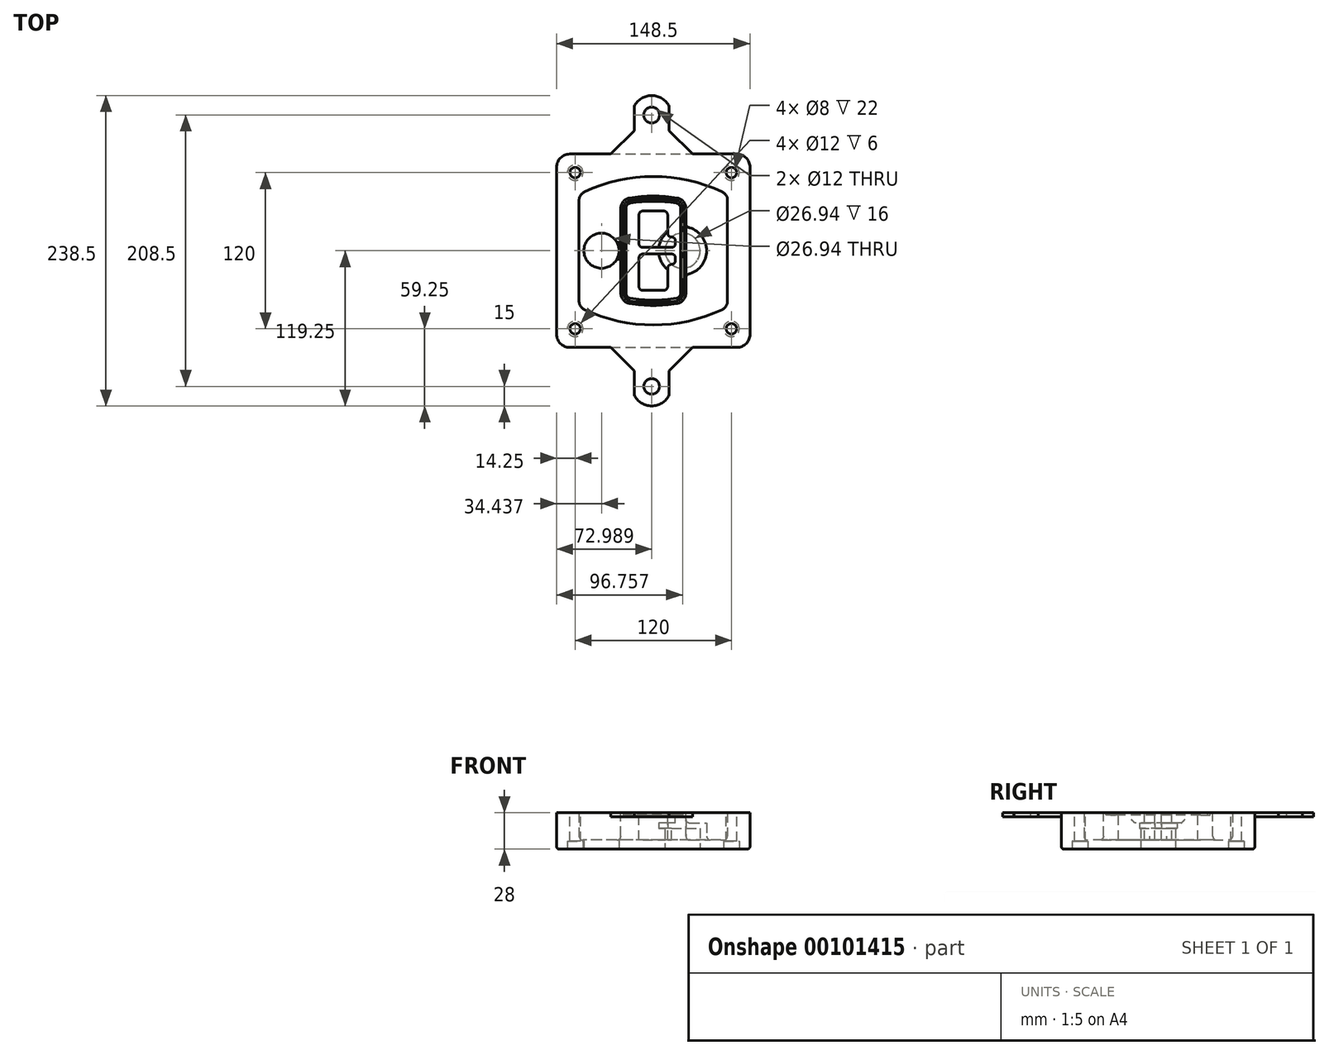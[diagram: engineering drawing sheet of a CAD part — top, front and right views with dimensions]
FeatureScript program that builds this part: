
annotation { "Feature Type Name" : "Feature", "Feature Type Description" : "" }
export const myFeature = defineFeature(function(context is Context, id is Id, definition is map)
    precondition{}
    {
        {
            var Q0;
            Q0=qCreatedBy(makeId("Top.planeOp"),FACE);
            var sketch = newSketch(context, id + "F0", { "sketchPlane" : qUnion([Q0])});
            skPoint(sketch, "E0.rect.middle", {"position": v(0, 0) * mm});
            skLineSegment(sketch, "E1.bottom", {"start": v(-64.25, -74.25) * mm, "end": v(64.25, -74.25) * mm});
            skLineSegment(sketch, "E1.top", {"start": v(-64.25, 74.25) * mm, "end": v(64.25, 74.25) * mm});
            skLineSegment(sketch, "E1.left", {"start": v(-74.25, -64.25) * mm, "end": v(-74.25, 64.25) * mm});
            skLineSegment(sketch, "E1.right", {"start": v(74.25, -64.25) * mm, "end": v(74.25, 64.25) * mm});
            skLineSegment(sketch, "E2", {"start": v(-74.25, 74.25) * mm, "end": v(74.25, -74.25) * mm, "construction": true});
            skLineSegment(sketch, "E3", {"start": v(74.25, 74.25) * mm, "end": v(-74.25, -74.25) * mm, "construction": true});
            skCircle(sketch, "E4", {"center": v(-60, 60) * mm, "radius": 4 * mm});
            skCircle(sketch, "E5", {"center": v(60, 60) * mm, "radius": 4 * mm});
            skCircle(sketch, "E6", {"center": v(60, -60) * mm, "radius": 4 * mm});
            skCircle(sketch, "E7", {"center": v(-60, -60) * mm, "radius": 4 * mm});
            skLineSegment(sketch, "E8", {"start": v(-60, 60) * mm, "end": v(60, 60) * mm, "construction": true});
            skLineSegment(sketch, "E9", {"start": v(60, 60) * mm, "end": v(60, -60) * mm, "construction": true});
            skLineSegment(sketch, "E10", {"start": v(60, -60) * mm, "end": v(-60, -60) * mm, "construction": true});
            skLineSegment(sketch, "E11", {"start": v(-60, -60) * mm, "end": v(-60, 60) * mm, "construction": true});
            skLineSegment(sketch, "E12", {"start": v(-60, 38.83) * mm, "end": v(-60, -38.83) * mm});
            skLineSegment(sketch, "E13", {"start": v(60, 38.83) * mm, "end": v(60, -38.83) * mm});
            skArc(sketch, "E14", {"start": v(54.26, 47.88) * mm, "mid": v(0, 60) * mm, "end": v(-54.26, 47.88) * mm});
            skArc(sketch, "E15", {"start": v(-54.26, -47.88) * mm, "mid": v(0, -60) * mm, "end": v(54.26, -47.88) * mm});
            skLineSegment(sketch, "E16", {"start": v(-60, 0) * mm, "end": v(60, 0) * mm, "construction": true});
            skPoint(sketch, "E17.visualSharp", {"position": v(-60, -45) * mm});
            skArc(sketch, "E17.filletArc", {"start": v(-60, -38.83) * mm, "mid": v(-58.44, -44.2) * mm, "end": v(-54.26, -47.88) * mm});
            skPoint(sketch, "E18.visualSharp", {"position": v(-60, 45) * mm});
            skArc(sketch, "E18.filletArc", {"start": v(-54.26, 47.88) * mm, "mid": v(-58.44, 44.2) * mm, "end": v(-60, 38.83) * mm});
            skPoint(sketch, "E19.visualSharp", {"position": v(60, 45) * mm});
            skArc(sketch, "E19.filletArc", {"start": v(60, 38.83) * mm, "mid": v(58.44, 44.2) * mm, "end": v(54.26, 47.88) * mm});
            skPoint(sketch, "E20.visualSharp", {"position": v(60, -45) * mm});
            skArc(sketch, "E20.filletArc", {"start": v(54.26, -47.88) * mm, "mid": v(58.44, -44.2) * mm, "end": v(60, -38.83) * mm});
            skPoint(sketch, "E21.visualSharp", {"position": v(-74.25, 74.25) * mm});
            skArc(sketch, "E21.filletArc", {"start": v(-64.25, 74.25) * mm, "mid": v(-71.32, 71.32) * mm, "end": v(-74.25, 64.25) * mm});
            skPoint(sketch, "E22.visualSharp", {"position": v(74.25, 74.25) * mm});
            skArc(sketch, "E22.filletArc", {"start": v(74.25, 64.25) * mm, "mid": v(71.32, 71.32) * mm, "end": v(64.25, 74.25) * mm});
            skPoint(sketch, "E23.visualSharp", {"position": v(74.25, -74.25) * mm});
            skArc(sketch, "E23.filletArc", {"start": v(64.25, -74.25) * mm, "mid": v(71.32, -71.32) * mm, "end": v(74.25, -64.25) * mm});
            skPoint(sketch, "E24.visualSharp", {"position": v(-74.25, -74.25) * mm});
            skArc(sketch, "E24.filletArc", {"start": v(-74.25, -64.25) * mm, "mid": v(-71.32, -71.32) * mm, "end": v(-64.25, -74.25) * mm});
            skArc(sketch, "E25.0", {"start": v(57, 38.83) * mm, "mid": v(55.9, 42.58) * mm, "end": v(52.98, 45.17) * mm});
            skLineSegment(sketch, "E25.1", {"start": v(57, 38.83) * mm, "end": v(57, -38.83) * mm});
            skArc(sketch, "E25.2", {"start": v(52.98, -45.17) * mm, "mid": v(55.9, -42.58) * mm, "end": v(57, -38.83) * mm});
            skArc(sketch, "E25.3", {"start": v(-52.98, -45.17) * mm, "mid": v(0, -57) * mm, "end": v(52.98, -45.17) * mm});
            skArc(sketch, "E25.4", {"start": v(-57, -38.83) * mm, "mid": v(-55.9, -42.58) * mm, "end": v(-52.98, -45.17) * mm});
            skArc(sketch, "E25.5", {"start": v(52.98, 45.17) * mm, "mid": v(0, 57) * mm, "end": v(-52.98, 45.17) * mm});
            skLineSegment(sketch, "E25.6", {"start": v(-57, 38.83) * mm, "end": v(-57, -38.83) * mm});
            skArc(sketch, "E25.7", {"start": v(-52.98, 45.17) * mm, "mid": v(-55.9, 42.58) * mm, "end": v(-57, 38.83) * mm});
            skArc(sketch, "E26.0", {"start": v(-55.96, 51.5) * mm, "mid": v(-61.82, 46.33) * mm, "end": v(-64, 38.83) * mm});
            skArc(sketch, "E26.1", {"start": v(55.96, 51.5) * mm, "mid": v(0, 64) * mm, "end": v(-55.96, 51.5) * mm});
            skArc(sketch, "E26.2", {"start": v(64, 38.83) * mm, "mid": v(61.82, 46.33) * mm, "end": v(55.96, 51.5) * mm});
            skLineSegment(sketch, "E26.3", {"start": v(64, 38.83) * mm, "end": v(64, -38.83) * mm});
            skArc(sketch, "E26.4", {"start": v(55.96, -51.5) * mm, "mid": v(61.82, -46.33) * mm, "end": v(64, -38.83) * mm});
            skLineSegment(sketch, "E26.5", {"start": v(-64, 38.83) * mm, "end": v(-64, -38.83) * mm});
            skArc(sketch, "E26.6", {"start": v(-55.96, -51.5) * mm, "mid": v(0, -64) * mm, "end": v(55.96, -51.5) * mm});
            skArc(sketch, "E26.7", {"start": v(-64, -38.83) * mm, "mid": v(-61.82, -46.33) * mm, "end": v(-55.96, -51.5) * mm});
            skSolve(sketch);
        }
        {
            var Q0;
            Q0=makeQuery(id+"F0.imprint","IMPRINT",FACE,{"disambiguationData":[TD([[makeQuery(id+"F0.imprint","IMPRINT",EDGE,{"derivedFrom":sQuery(id+"F0.wireOp",EDGE,"E1.bottom")}),1.0]])]});
            var Q1;
            Q1=makeQuery(id+"F0.imprint","IMPRINT",FACE,{"disambiguationData":[TD([[makeQuery(id+"F0.imprint","IMPRINT",EDGE,{"derivedFrom":sQuery(id+"F0.wireOp",EDGE,"E12")}),1.0]])]});
            var Q2;
            Q2=makeQuery(id+"F0.imprint","IMPRINT",FACE,{"disambiguationData":[TD([[makeQuery(id+"F0.imprint","IMPRINT",EDGE,{"derivedFrom":sQuery(id+"F0.wireOp",EDGE,"E25.0")}),1.0]])]});
            var Q3;
            Q3=makeQuery(id+"F0.imprint","IMPRINT",FACE,{"disambiguationData":[TD([[makeQuery(id+"F0.imprint","IMPRINT",EDGE,{"derivedFrom":sQuery(id+"F0.wireOp",EDGE,"E12")}),-1.0]])]});
            extrude(context, id + "F1", {"entities" : qUnion([Q0, Q1, Q2, Q3]), "oppositeDirection" : true, "depth" : 25 * mm});
        }
        {
            var Q0;
            Q0=makeQuery(id+"F0.imprint","IMPRINT",FACE,{"disambiguationData":[TD([[makeQuery(id+"F0.imprint","IMPRINT",EDGE,{"derivedFrom":sQuery(id+"F0.wireOp",EDGE,"E12")}),1.0]])]});
            extrude(context, id + "F2", {"entities" : qUnion([Q0]), "operationType" : NewBodyOperationType.ADD, "depth" : 3 * mm});
        }
        {
            var Q0;
            Q0=makeQuery(id+"F0.imprint","IMPRINT",FACE,{"disambiguationData":[TD([[makeQuery(id+"F0.imprint","IMPRINT",EDGE,{"derivedFrom":sQuery(id+"F0.wireOp",EDGE,"E25.0")}),1.0]])]});
            extrude(context, id + "F3", {"entities" : qUnion([Q0]), "operationType" : NewBodyOperationType.REMOVE, "oppositeDirection" : true, "depth" : 18 * mm});
        }
        {
            var Q0;
            Q0=makeQuery(id+"F2.opExtrude","CAP_FACE",FACE,{"disambiguationData":[OSD([sQuery(id+"F0.wireOp",EDGE,"E12"),sQuery(id+"F0.wireOp",EDGE,"E13"),sQuery(id+"F0.wireOp",EDGE,"E14"),sQuery(id+"F0.wireOp",EDGE,"E15"),sQuery(id+"F0.wireOp",EDGE,"E17.filletArc"),sQuery(id+"F0.wireOp",EDGE,"E18.filletArc"),sQuery(id+"F0.wireOp",EDGE,"E19.filletArc"),sQuery(id+"F0.wireOp",EDGE,"E20.filletArc"),sQuery(id+"F0.wireOp",EDGE,"E25.0"),sQuery(id+"F0.wireOp",EDGE,"E25.1"),sQuery(id+"F0.wireOp",EDGE,"E25.2"),sQuery(id+"F0.wireOp",EDGE,"E25.3"),sQuery(id+"F0.wireOp",EDGE,"E25.4"),sQuery(id+"F0.wireOp",EDGE,"E25.5"),sQuery(id+"F0.wireOp",EDGE,"E25.6"),sQuery(id+"F0.wireOp",EDGE,"E25.7")])],"isStart":false});
            var sketch = newSketch(context, id + "F4", { "sketchPlane" : qUnion([Q0])});
            skArc(sketch, "E27.0", {"start": v(-18.34, -40.45) * mm, "mid": v(0, -42) * mm, "end": v(18.34, -40.45) * mm});
            skArc(sketch, "E28.0", {"start": v(18.34, 40.45) * mm, "mid": v(0, 42) * mm, "end": v(-18.34, 40.45) * mm});
            skLineSegment(sketch, "E29", {"start": v(-25, 32.57) * mm, "end": v(-25, -32.57) * mm});
            skLineSegment(sketch, "E30", {"start": v(25, 32.57) * mm, "end": v(25, -32.57) * mm});
            skLineSegment(sketch, "E31", {"start": v(-25, 39.1) * mm, "end": v(25, 39.1) * mm, "construction": true});
            skLineSegment(sketch, "E32", {"start": v(-25, -39.1) * mm, "end": v(25, -39.1) * mm, "construction": true});
            skPoint(sketch, "E33.visualSharp", {"position": v(-25, 39.1) * mm});
            skArc(sketch, "E33.filletArc", {"start": v(-18.34, 40.45) * mm, "mid": v(-23.11, 37.73) * mm, "end": v(-25, 32.57) * mm});
            skPoint(sketch, "E34.visualSharp", {"position": v(25, 39.1) * mm});
            skArc(sketch, "E34.filletArc", {"start": v(25, 32.57) * mm, "mid": v(23.11, 37.73) * mm, "end": v(18.34, 40.45) * mm});
            skPoint(sketch, "E35.visualSharp", {"position": v(25, -39.1) * mm});
            skArc(sketch, "E35.filletArc", {"start": v(18.34, -40.45) * mm, "mid": v(23.11, -37.73) * mm, "end": v(25, -32.57) * mm});
            skPoint(sketch, "E36.visualSharp", {"position": v(-25, -39.1) * mm});
            skArc(sketch, "E36.filletArc", {"start": v(-25, -32.57) * mm, "mid": v(-23.11, -37.73) * mm, "end": v(-18.34, -40.45) * mm});
            skArc(sketch, "E37.0", {"start": v(52.98, 45.17) * mm, "mid": v(0, 57) * mm, "end": v(-52.98, 45.17) * mm});
            skArc(sketch, "E37.1", {"start": v(-52.98, 45.17) * mm, "mid": v(-55.9, 42.58) * mm, "end": v(-57, 38.83) * mm});
            skLineSegment(sketch, "E37.2", {"start": v(-57, 38.83) * mm, "end": v(-57, -38.83) * mm});
            skArc(sketch, "E37.3", {"start": v(-57, -38.83) * mm, "mid": v(-55.9, -42.58) * mm, "end": v(-52.98, -45.17) * mm});
            skArc(sketch, "E37.4", {"start": v(-52.98, -45.17) * mm, "mid": v(0, -57) * mm, "end": v(52.98, -45.17) * mm});
            skArc(sketch, "E37.5", {"start": v(52.98, -45.17) * mm, "mid": v(55.9, -42.58) * mm, "end": v(57, -38.83) * mm});
            skLineSegment(sketch, "E37.6", {"start": v(57, 38.83) * mm, "end": v(57, -38.83) * mm});
            skArc(sketch, "E37.7", {"start": v(57, 38.83) * mm, "mid": v(55.9, 42.58) * mm, "end": v(52.98, 45.17) * mm});
            skLineSegment(sketch, "E38.0", {"start": v(23, 32.57) * mm, "end": v(23, -32.57) * mm});
            skArc(sketch, "E38.1", {"start": v(18, -38.48) * mm, "mid": v(21.58, -36.44) * mm, "end": v(23, -32.57) * mm});
            skArc(sketch, "E38.2", {"start": v(-18, -38.48) * mm, "mid": v(0, -40) * mm, "end": v(18, -38.48) * mm});
            skArc(sketch, "E38.3", {"start": v(-23, -32.57) * mm, "mid": v(-21.58, -36.44) * mm, "end": v(-18, -38.48) * mm});
            skLineSegment(sketch, "E38.4", {"start": v(-23, 32.57) * mm, "end": v(-23, -32.57) * mm});
            skArc(sketch, "E38.5", {"start": v(23, 32.57) * mm, "mid": v(21.58, 36.44) * mm, "end": v(18, 38.48) * mm});
            skArc(sketch, "E38.6", {"start": v(-18, 38.48) * mm, "mid": v(-21.58, 36.44) * mm, "end": v(-23, 32.57) * mm});
            skArc(sketch, "E38.7", {"start": v(18, 38.48) * mm, "mid": v(0, 40) * mm, "end": v(-18, 38.48) * mm});
            skArc(sketch, "E39.0", {"start": v(21, 32.57) * mm, "mid": v(20.06, 35.15) * mm, "end": v(17.67, 36.5) * mm});
            skLineSegment(sketch, "E39.1", {"start": v(21, 32.57) * mm, "end": v(21, -32.57) * mm});
            skArc(sketch, "E39.2", {"start": v(17.67, -36.5) * mm, "mid": v(20.06, -35.15) * mm, "end": v(21, -32.57) * mm});
            skArc(sketch, "E39.3", {"start": v(-17.67, -36.5) * mm, "mid": v(0, -38) * mm, "end": v(17.67, -36.5) * mm});
            skArc(sketch, "E39.4", {"start": v(-21, -32.57) * mm, "mid": v(-20.06, -35.15) * mm, "end": v(-17.67, -36.5) * mm});
            skArc(sketch, "E39.5", {"start": v(17.67, 36.5) * mm, "mid": v(0, 38) * mm, "end": v(-17.67, 36.5) * mm});
            skLineSegment(sketch, "E39.6", {"start": v(-21, 32.57) * mm, "end": v(-21, -32.57) * mm});
            skArc(sketch, "E39.7", {"start": v(-17.67, 36.5) * mm, "mid": v(-20.06, 35.15) * mm, "end": v(-21, 32.57) * mm});
            skLineSegment(sketch, "E40", {"start": v(-25, 0) * mm, "end": v(25, 0) * mm, "construction": true});
            skLineSegment(sketch, "E41", {"start": v(-11, 5.5) * mm, "end": v(-11, 27.5) * mm});
            skLineSegment(sketch, "E42", {"start": v(-8, 30.5) * mm, "end": v(8, 30.5) * mm});
            skLineSegment(sketch, "E43", {"start": v(11, 27.5) * mm, "end": v(11, 13.5) * mm});
            skLineSegment(sketch, "E44", {"start": v(14, 10.5) * mm, "end": v(14, 10.5) * mm});
            skLineSegment(sketch, "E45", {"start": v(17, 7.5) * mm, "end": v(17, 5.5) * mm});
            skLineSegment(sketch, "E46", {"start": v(14, 2.5) * mm, "end": v(-8, 2.5) * mm});
            skPoint(sketch, "E47.visualSharp", {"position": v(-11, 30.5) * mm});
            skArc(sketch, "E47.filletArc", {"start": v(-8, 30.5) * mm, "mid": v(-10.12, 29.62) * mm, "end": v(-11, 27.5) * mm});
            skPoint(sketch, "E48.visualSharp", {"position": v(11, 30.5) * mm});
            skArc(sketch, "E48.filletArc", {"start": v(11, 27.5) * mm, "mid": v(10.12, 29.62) * mm, "end": v(8, 30.5) * mm});
            skPoint(sketch, "E49.visualSharp", {"position": v(11, 10.5) * mm});
            skArc(sketch, "E49.filletArc", {"start": v(11, 13.5) * mm, "mid": v(11.88, 11.38) * mm, "end": v(14, 10.5) * mm});
            skPoint(sketch, "E50.visualSharp", {"position": v(17, 10.5) * mm});
            skArc(sketch, "E50.filletArc", {"start": v(17, 7.5) * mm, "mid": v(16.12, 9.62) * mm, "end": v(14, 10.5) * mm});
            skPoint(sketch, "E51.visualSharp", {"position": v(17, 2.5) * mm});
            skArc(sketch, "E51.filletArc", {"start": v(14, 2.5) * mm, "mid": v(16.12, 3.38) * mm, "end": v(17, 5.5) * mm});
            skPoint(sketch, "E52.visualSharp", {"position": v(-11, 2.5) * mm});
            skArc(sketch, "E52.filletArc", {"start": v(-11, 5.5) * mm, "mid": v(-10.12, 3.38) * mm, "end": v(-8, 2.5) * mm});
            skLineSegment(sketch, "E53.0.MirrorCS", {"start": v(14, -2.5) * mm, "end": v(-8, -2.5) * mm});
            skArc(sketch, "E54.0.MirrorCS", {"start": v(-11, -5.5) * mm, "mid": v(-10.12, -3.38) * mm, "end": v(-8, -2.5) * mm});
            skLineSegment(sketch, "E55.0.MirrorCS", {"start": v(-11, -5.5) * mm, "end": v(-11, -27.5) * mm});
            skArc(sketch, "E56.0.MirrorCS", {"start": v(-8, -30.5) * mm, "mid": v(-10.12, -29.62) * mm, "end": v(-11, -27.5) * mm});
            skLineSegment(sketch, "E57.0.MirrorCS", {"start": v(-8, -30.5) * mm, "end": v(8, -30.5) * mm});
            skArc(sketch, "E58.0.MirrorCS", {"start": v(11, -27.5) * mm, "mid": v(10.12, -29.62) * mm, "end": v(8, -30.5) * mm});
            skLineSegment(sketch, "E59.0.MirrorCS", {"start": v(11, -27.5) * mm, "end": v(11, -13.5) * mm});
            skArc(sketch, "E60.0.MirrorCS", {"start": v(11, -13.5) * mm, "mid": v(11.88, -11.38) * mm, "end": v(14, -10.5) * mm});
            skArc(sketch, "E61.0.MirrorCS", {"start": v(17, -7.5) * mm, "mid": v(16.12, -9.62) * mm, "end": v(14, -10.5) * mm});
            skLineSegment(sketch, "E62.0.MirrorCS", {"start": v(17, -7.5) * mm, "end": v(17, -5.5) * mm});
            skArc(sketch, "E63.0.MirrorCS", {"start": v(14, -2.5) * mm, "mid": v(16.12, -3.38) * mm, "end": v(17, -5.5) * mm});
            skSolve(sketch);
        }
        {
            var Q0;
            Q0=makeQuery(id+"F4.imprint","IMPRINT",FACE,{"disambiguationData":[TD([[makeQuery(id+"F4.imprint","IMPRINT",EDGE,{"derivedFrom":sQuery(id+"F4.wireOp",EDGE,"E27.0")}),1.0]])]});
            var Q1;
            Q1=makeQuery(id+"F4.imprint","IMPRINT",FACE,{"disambiguationData":[TD([[makeQuery(id+"F4.imprint","IMPRINT",EDGE,{"derivedFrom":sQuery(id+"F4.wireOp",EDGE,"E38.0")}),-1.0]])]});
            var Q2;
            Q2=makeQuery(id+"F4.imprint","IMPRINT",FACE,{"disambiguationData":[TD([[makeQuery(id+"F4.imprint","IMPRINT",EDGE,{"derivedFrom":sQuery(id+"F4.wireOp",EDGE,"E39.0")}),1.0]])]});
            extrude(context, id + "F5", {"entities" : qUnion([Q0, Q1, Q2]), "operationType" : NewBodyOperationType.ADD, "endBound" : BoundingType.UP_TO_NEXT, "oppositeDirection" : true, "depth" : 25 * mm});
        }
        {
            var Q0;
            Q0=makeQuery(id+"F4.imprint","IMPRINT",FACE,{"disambiguationData":[TD([[makeQuery(id+"F4.imprint","IMPRINT",EDGE,{"derivedFrom":sQuery(id+"F4.wireOp",EDGE,"E38.0")}),-1.0]])]});
            extrude(context, id + "F6", {"entities" : qUnion([Q0]), "operationType" : NewBodyOperationType.REMOVE, "oppositeDirection" : true, "depth" : 2 * mm});
        }
        {
            var Q0;
            Q0=makeQuery(id+"F1.opExtrude","CAP_FACE",FACE,{"disambiguationData":[OSD([sQuery(id+"F0.wireOp",EDGE,"E1.bottom"),sQuery(id+"F0.wireOp",EDGE,"E1.top"),sQuery(id+"F0.wireOp",EDGE,"E1.left"),sQuery(id+"F0.wireOp",EDGE,"E1.right"),sQuery(id+"F0.wireOp",EDGE,"E4"),sQuery(id+"F0.wireOp",EDGE,"E5"),sQuery(id+"F0.wireOp",EDGE,"E6"),sQuery(id+"F0.wireOp",EDGE,"E7"),sQuery(id+"F0.wireOp",EDGE,"E21.filletArc"),sQuery(id+"F0.wireOp",EDGE,"E22.filletArc"),sQuery(id+"F0.wireOp",EDGE,"E23.filletArc"),sQuery(id+"F0.wireOp",EDGE,"E24.filletArc")])],"isStart":false});
            var sketch = newSketch(context, id + "F7", { "sketchPlane" : qUnion([Q0])});
            skCircle(sketch, "E64", {"center": v(22.5, 0) * mm, "radius": 13.47 * mm});
            skCircle(sketch, "E65", {"center": v(-39.81, 0) * mm, "radius": 13.47 * mm});
            skLineSegment(sketch, "E66", {"start": v(74.25, 0) * mm, "end": v(-74.25, 0) * mm});
            skCircle(sketch, "E67", {"center": v(22.5, 0) * mm, "radius": 18.47 * mm});
            skCircle(sketch, "E68", {"center": v(60, -60) * mm, "radius": 6 * mm});
            skCircle(sketch, "E69", {"center": v(-60, -60) * mm, "radius": 6 * mm});
            skCircle(sketch, "E70", {"center": v(-60, 60) * mm, "radius": 6 * mm});
            skCircle(sketch, "E71", {"center": v(60, 60) * mm, "radius": 6 * mm});
            skSolve(sketch);
        }
        {
            var Q0;
            {var subQ1=sQuery(id+"F7.wireOp",EDGE,"E66");var subQ4=sQuery(id+"F7.wireOp",EDGE,"E64");var subQ6=makeQuery(id+"F7.imprint","INTERSECT",VERTEX,{"disambiguationData":[OD(0.0)],"derivedFrom":[subQ4,subQ1]});Q0=makeQuery(id+"F7.imprint","IMPRINT",FACE,{"disambiguationData":[TD([[makeQuery(id+"F7.imprint","IMPRINT",EDGE,{"disambiguationData":[TD([[subQ6,-1.0]])],"derivedFrom":subQ4}),-1.0]])]});}
            var Q1;
            {var subQ0=sQuery(id+"F7.wireOp",EDGE,"E66");var subQ1=sQuery(id+"F7.wireOp",EDGE,"E64");var subQ3=makeQuery(id+"F7.imprint","INTERSECT",VERTEX,{"disambiguationData":[OD(0.0)],"derivedFrom":[subQ1,subQ0]});Q1=makeQuery(id+"F7.imprint","IMPRINT",FACE,{"disambiguationData":[TD([[makeQuery(id+"F7.imprint","IMPRINT",EDGE,{"disambiguationData":[TD([[subQ3,-1.0]])],"derivedFrom":subQ1}),1.0]])]});}
            var Q2;
            {var subQ0=sQuery(id+"F7.wireOp",EDGE,"E66");var subQ1=sQuery(id+"F7.wireOp",EDGE,"E64");var subQ3=makeQuery(id+"F7.imprint","INTERSECT",VERTEX,{"disambiguationData":[OD(0.0)],"derivedFrom":[subQ1,subQ0]});Q2=makeQuery(id+"F7.imprint","IMPRINT",FACE,{"disambiguationData":[TD([[makeQuery(id+"F7.imprint","IMPRINT",EDGE,{"disambiguationData":[TD([[subQ3,1.0]])],"derivedFrom":subQ1}),1.0]])]});}
            var Q3;
            {var subQ1=sQuery(id+"F7.wireOp",EDGE,"E66");var subQ4=sQuery(id+"F7.wireOp",EDGE,"E64");var subQ6=makeQuery(id+"F7.imprint","INTERSECT",VERTEX,{"disambiguationData":[OD(0.0)],"derivedFrom":[subQ4,subQ1]});Q3=makeQuery(id+"F7.imprint","IMPRINT",FACE,{"disambiguationData":[TD([[makeQuery(id+"F7.imprint","IMPRINT",EDGE,{"disambiguationData":[TD([[subQ6,1.0]])],"derivedFrom":subQ4}),-1.0]])]});}
            extrude(context, id + "F8", {"entities" : qUnion([Q0, Q1, Q2, Q3]), "operationType" : NewBodyOperationType.ADD, "oppositeDirection" : true, "depth" : 20 * mm});
        }
        {
            var Q0;
            {var subQ0=sQuery(id+"F7.wireOp",EDGE,"E66");var subQ1=sQuery(id+"F7.wireOp",EDGE,"E64");var subQ3=makeQuery(id+"F7.imprint","INTERSECT",VERTEX,{"disambiguationData":[OD(0.0)],"derivedFrom":[subQ1,subQ0]});Q0=makeQuery(id+"F7.imprint","IMPRINT",FACE,{"disambiguationData":[TD([[makeQuery(id+"F7.imprint","IMPRINT",EDGE,{"disambiguationData":[TD([[subQ3,-1.0]])],"derivedFrom":subQ1}),1.0]])]});}
            var Q1;
            {var subQ0=sQuery(id+"F7.wireOp",EDGE,"E66");var subQ1=sQuery(id+"F7.wireOp",EDGE,"E64");var subQ3=makeQuery(id+"F7.imprint","INTERSECT",VERTEX,{"disambiguationData":[OD(0.0)],"derivedFrom":[subQ1,subQ0]});Q1=makeQuery(id+"F7.imprint","IMPRINT",FACE,{"disambiguationData":[TD([[makeQuery(id+"F7.imprint","IMPRINT",EDGE,{"disambiguationData":[TD([[subQ3,1.0]])],"derivedFrom":subQ1}),1.0]])]});}
            extrude(context, id + "F9", {"entities" : qUnion([Q0, Q1]), "operationType" : NewBodyOperationType.REMOVE, "oppositeDirection" : true, "depth" : 16 * mm});
        }
        {
            var Q0;
            {var subQ0=sQuery(id+"F7.wireOp",EDGE,"E66");var subQ1=sQuery(id+"F7.wireOp",EDGE,"E65");var subQ3=makeQuery(id+"F7.imprint","INTERSECT",VERTEX,{"disambiguationData":[OD(0.0)],"derivedFrom":[subQ1,subQ0]});Q0=makeQuery(id+"F7.imprint","IMPRINT",FACE,{"disambiguationData":[TD([[makeQuery(id+"F7.imprint","IMPRINT",EDGE,{"disambiguationData":[TD([[subQ3,-1.0]])],"derivedFrom":subQ1}),1.0]])]});}
            var Q1;
            {var subQ0=sQuery(id+"F7.wireOp",EDGE,"E66");var subQ1=sQuery(id+"F7.wireOp",EDGE,"E65");var subQ3=makeQuery(id+"F7.imprint","INTERSECT",VERTEX,{"disambiguationData":[OD(0.0)],"derivedFrom":[subQ1,subQ0]});Q1=makeQuery(id+"F7.imprint","IMPRINT",FACE,{"disambiguationData":[TD([[makeQuery(id+"F7.imprint","IMPRINT",EDGE,{"disambiguationData":[TD([[subQ3,1.0]])],"derivedFrom":subQ1}),1.0]])]});}
            extrude(context, id + "F10", {"entities" : qUnion([Q0, Q1]), "operationType" : NewBodyOperationType.REMOVE, "oppositeDirection" : true, "depth" : 25 * mm});
        }
        {
            var Q0;
            Q0=makeQuery(id+"F7.imprint","IMPRINT",FACE,{"disambiguationData":[TD([[makeQuery(id+"F7.imprint","IMPRINT",EDGE,{"derivedFrom":sQuery(id+"F7.wireOp",EDGE,"E68")}),1.0]])]});
            var Q1;
            Q1=makeQuery(id+"F7.imprint","IMPRINT",FACE,{"disambiguationData":[TD([[makeQuery(id+"F7.imprint","IMPRINT",EDGE,{"derivedFrom":makeQuery(id+"F1.opExtrude","CAP_EDGE",EDGE,{"disambiguationData":[OSD([sQuery(id+"F0.wireOp",EDGE,"E5")])],"isStart":false})}),-1.0]])]});
            var Q2;
            Q2=makeQuery(id+"F7.imprint","IMPRINT",FACE,{"disambiguationData":[TD([[makeQuery(id+"F7.imprint","IMPRINT",EDGE,{"derivedFrom":sQuery(id+"F7.wireOp",EDGE,"E69")}),1.0]])]});
            var Q3;
            Q3=makeQuery(id+"F7.imprint","IMPRINT",FACE,{"disambiguationData":[TD([[makeQuery(id+"F7.imprint","IMPRINT",EDGE,{"derivedFrom":makeQuery(id+"F1.opExtrude","CAP_EDGE",EDGE,{"disambiguationData":[OSD([sQuery(id+"F0.wireOp",EDGE,"E4")])],"isStart":false})}),-1.0]])]});
            var Q4;
            Q4=makeQuery(id+"F7.imprint","IMPRINT",FACE,{"disambiguationData":[TD([[makeQuery(id+"F7.imprint","IMPRINT",EDGE,{"derivedFrom":sQuery(id+"F7.wireOp",EDGE,"E70")}),1.0]])]});
            var Q5;
            Q5=makeQuery(id+"F7.imprint","IMPRINT",FACE,{"disambiguationData":[TD([[makeQuery(id+"F7.imprint","IMPRINT",EDGE,{"derivedFrom":makeQuery(id+"F1.opExtrude","CAP_EDGE",EDGE,{"disambiguationData":[OSD([sQuery(id+"F0.wireOp",EDGE,"E7")])],"isStart":false})}),-1.0]])]});
            var Q6;
            Q6=makeQuery(id+"F7.imprint","IMPRINT",FACE,{"disambiguationData":[TD([[makeQuery(id+"F7.imprint","IMPRINT",EDGE,{"derivedFrom":sQuery(id+"F7.wireOp",EDGE,"E71")}),1.0]])]});
            var Q7;
            Q7=makeQuery(id+"F7.imprint","IMPRINT",FACE,{"disambiguationData":[TD([[makeQuery(id+"F7.imprint","IMPRINT",EDGE,{"derivedFrom":makeQuery(id+"F1.opExtrude","CAP_EDGE",EDGE,{"disambiguationData":[OSD([sQuery(id+"F0.wireOp",EDGE,"E6")])],"isStart":false})}),-1.0]])]});
            extrude(context, id + "F11", {"entities" : qUnion([Q0, Q1, Q2, Q3, Q4, Q5, Q6, Q7]), "operationType" : NewBodyOperationType.REMOVE, "oppositeDirection" : true, "depth" : 6 * mm});
        }
        {
            var Q0;
            Q0=makeQuery(id+"F9.boolean.opBoolean","COPY",FACE,{"derivedFrom":makeQuery(id+"F9.opExtrude","CAP_FACE",FACE,{"disambiguationData":[OSD([sQuery(id+"F7.wireOp",EDGE,"E64")])],"isStart":false})});
            var sketch = newSketch(context, id + "F12", { "sketchPlane" : qUnion([Q0])});
            skArc(sketch, "E72.0", {"start": v(11, 14.45) * mm, "mid": v(6.45, 9.13) * mm, "end": v(4.2, 2.5) * mm});
            skArc(sketch, "E72.1", {"start": v(4.2, -2.5) * mm, "mid": v(6.45, -9.13) * mm, "end": v(11, -14.45) * mm});
            skLineSegment(sketch, "E73", {"start": v(4.2, -2.5) * mm, "end": v(14, -2.5) * mm});
            skLineSegment(sketch, "E74.0", {"start": v(14, 2.5) * mm, "end": v(4.2, 2.5) * mm});
            skArc(sketch, "E74.1", {"start": v(14, 2.5) * mm, "mid": v(16.12, 3.38) * mm, "end": v(17, 5.5) * mm});
            skLineSegment(sketch, "E74.2", {"start": v(17, 7.5) * mm, "end": v(17, 5.5) * mm});
            skArc(sketch, "E74.3", {"start": v(17, 7.5) * mm, "mid": v(16.12, 9.62) * mm, "end": v(14, 10.5) * mm});
            skArc(sketch, "E74.4", {"start": v(11, 13.5) * mm, "mid": v(11.88, 11.38) * mm, "end": v(14, 10.5) * mm});
            skLineSegment(sketch, "E74.5", {"start": v(11, 14.45) * mm, "end": v(11, 13.5) * mm});
            skLineSegment(sketch, "E74.7", {"start": v(14, -2.5) * mm, "end": v(4.2, -2.5) * mm});
            skArc(sketch, "E74.8", {"start": v(14, -2.5) * mm, "mid": v(16.12, -3.38) * mm, "end": v(17, -5.5) * mm});
            skLineSegment(sketch, "E74.9", {"start": v(17, -7.5) * mm, "end": v(17, -5.5) * mm});
            skArc(sketch, "E74.10", {"start": v(17, -7.5) * mm, "mid": v(16.12, -9.62) * mm, "end": v(14, -10.5) * mm});
            skArc(sketch, "E74.11", {"start": v(11, -13.5) * mm, "mid": v(11.88, -11.38) * mm, "end": v(14, -10.5) * mm});
            skLineSegment(sketch, "E74.12", {"start": v(11, -14.45) * mm, "end": v(11, -13.5) * mm});
            skPoint(sketch, "E75.orphan", {"position": v(11, -27.5) * mm});
            skPoint(sketch, "E76.orphan", {"position": v(-8, -2.5) * mm});
            skPoint(sketch, "E77.orphan", {"position": v(-8, 2.5) * mm});
            skPoint(sketch, "E78.orphan", {"position": v(11, 27.5) * mm});
            skSolve(sketch);
        }
        {
            var Q0;
            {var subQ7=sQuery(id+"F12.wireOp",EDGE,"E72.0");var subQ14=sQuery(id+"F12.wireOp",EDGE,"E72.1");var subQ16=sQuery(id+"F12.wireOp",EDGE,"E74.1");var subQ18=sQuery(id+"F12.wireOp",EDGE,"E74.8");Q0=qUnion([makeQuery(id+"F12.imprint","IMPRINT",FACE,{"disambiguationData":[TD([[makeQuery(id+"F12.imprint","IMPRINT",EDGE,{"derivedFrom":subQ7}),1.0]])]}),makeQuery(id+"F12.imprint","IMPRINT",FACE,{"disambiguationData":[TD([[makeQuery(id+"F12.imprint","IMPRINT",EDGE,{"derivedFrom":subQ14}),1.0]])]}),makeQuery(id+"F12.imprint","IMPRINT",FACE,{"disambiguationData":[TD([[makeQuery(id+"F12.imprint","IMPRINT",EDGE,{"derivedFrom":subQ16}),1.0]])]}),makeQuery(id+"F12.imprint","IMPRINT",FACE,{"disambiguationData":[TD([[makeQuery(id+"F12.imprint","IMPRINT",EDGE,{"derivedFrom":subQ18}),-1.0]])]})]);}
            var Q1;
            Q1=makeQuery(id+"F5.boolean.opBoolean","SPLIT",FACE,{"disambiguationData":[TD([makeQuery(id+"F5.opExtrude","SWEPT_FACE",FACE,{"disambiguationData":[OSD([sQuery(id+"F4.wireOp",EDGE,"E41")])]})])],"derivedFrom":makeQuery(id+"F3.boolean.opBoolean","COPY",FACE,{"derivedFrom":makeQuery(id+"F3.opExtrude","CAP_FACE",FACE,{"disambiguationData":[OSD([sQuery(id+"F0.wireOp",EDGE,"E25.0"),sQuery(id+"F0.wireOp",EDGE,"E25.1"),sQuery(id+"F0.wireOp",EDGE,"E25.2"),sQuery(id+"F0.wireOp",EDGE,"E25.3"),sQuery(id+"F0.wireOp",EDGE,"E25.4"),sQuery(id+"F0.wireOp",EDGE,"E25.5"),sQuery(id+"F0.wireOp",EDGE,"E25.6"),sQuery(id+"F0.wireOp",EDGE,"E25.7")])],"isStart":false})})});
            extrude(context, id + "F13", {"entities" : qUnion([Q0]), "operationType" : NewBodyOperationType.REMOVE, "endBound" : BoundingType.UP_TO_SURFACE, "endBoundEntityFace" : qUnion([Q1]), "depth" : 25 * mm});
        }
        {
            var Q0;
            Q0=makeQuery(id+"F3.boolean.opBoolean","COPY",EDGE,{"derivedFrom":makeQuery(id+"F3.opExtrude","CAP_EDGE",EDGE,{"disambiguationData":[OSD([sQuery(id+"F0.wireOp",EDGE,"E25.6")])],"isStart":false})});
            var Q1;
            Q1=makeQuery(id+"F8.boolean.opBoolean","INTERSECT",EDGE,{"derivedFrom":[makeQuery(id+"F5.opExtrude","SWEPT_FACE",FACE,{"disambiguationData":[OSD([sQuery(id+"F4.wireOp",EDGE,"E30")])]}),makeQuery(id+"F8.opExtrude","CAP_FACE",FACE,{"disambiguationData":[OSD([sQuery(id+"F7.wireOp",EDGE,"E67")])],"isStart":false})]});
            var Q2;
            Q2=makeQuery(id+"F8.boolean.opBoolean","INTERSECT",EDGE,{"disambiguationData":[OD(1.0)],"derivedFrom":[makeQuery(id+"F5.opExtrude","SWEPT_FACE",FACE,{"disambiguationData":[OSD([sQuery(id+"F4.wireOp",EDGE,"E30")])]}),makeQuery(id+"F8.opExtrude","SWEPT_FACE",FACE,{"disambiguationData":[OSD([sQuery(id+"F7.wireOp",EDGE,"E67")])]})]});
            var Q3;
            {var subQ0=sQuery(id+"F4.wireOp",EDGE,"E30");Q3=makeQuery(id+"F8.boolean.opBoolean","SPLIT",EDGE,{"disambiguationData":[TD([makeQuery(id+"F5.opExtrude","SWEPT_FACE",FACE,{"disambiguationData":[OSD([sQuery(id+"F4.wireOp",EDGE,"E35.filletArc")])]})])],"derivedFrom":makeQuery(id+"F5.opExtrude","CAP_EDGE",EDGE,{"disambiguationData":[OSD([subQ0])],"isStart":false})});}
            var Q4;
            {var subQ0=sQuery(id+"F0.wireOp",EDGE,"E25.7");var subQ1=sQuery(id+"F0.wireOp",EDGE,"E25.1");var subQ2=sQuery(id+"F0.wireOp",EDGE,"E25.6");var subQ3=sQuery(id+"F0.wireOp",EDGE,"E25.5");var subQ4=sQuery(id+"F0.wireOp",EDGE,"E25.4");var subQ5=sQuery(id+"F0.wireOp",EDGE,"E25.0");var subQ6=sQuery(id+"F0.wireOp",EDGE,"E25.2");var subQ7=sQuery(id+"F0.wireOp",EDGE,"E25.3");Q4=makeQuery(id+"F8.boolean.opBoolean","INTERSECT",EDGE,{"derivedFrom":[makeQuery(id+"F5.boolean.opBoolean","SPLIT",FACE,{"disambiguationData":[TD([makeQuery(id+"F2.opExtrude","SWEPT_FACE",FACE,{"disambiguationData":[OSD([subQ5])]})])],"derivedFrom":makeQuery(id+"F3.boolean.opBoolean","COPY",FACE,{"derivedFrom":makeQuery(id+"F3.opExtrude","CAP_FACE",FACE,{"disambiguationData":[OSD([subQ5,subQ1,subQ6,subQ7,subQ4,subQ3,subQ2,subQ0])],"isStart":false})})}),makeQuery(id+"F8.opExtrude","SWEPT_FACE",FACE,{"disambiguationData":[OSD([sQuery(id+"F7.wireOp",EDGE,"E67")])]})]});}
            var Q5;
            Q5=makeQuery(id+"F8.boolean.opBoolean","INTERSECT",EDGE,{"disambiguationData":[OD(0.0)],"derivedFrom":[makeQuery(id+"F5.opExtrude","SWEPT_FACE",FACE,{"disambiguationData":[OSD([sQuery(id+"F4.wireOp",EDGE,"E30")])]}),makeQuery(id+"F8.opExtrude","SWEPT_FACE",FACE,{"disambiguationData":[OSD([sQuery(id+"F7.wireOp",EDGE,"E67")])]})]});
            fillet(context, id + "F14", {"entities" : qUnion([Q0, Q1, Q2, Q3, Q4, Q5]), "radius" : 3 * mm, "tangentPropagation" : true, "allowEdgeOverflow" : false});
        }
        {
            var Q0;
            Q0=makeQuery(id+"F1.opExtrude","CAP_EDGE",EDGE,{"disambiguationData":[OSD([sQuery(id+"F0.wireOp",EDGE,"E1.bottom")])],"isStart":false});
            fillet(context, id + "F15", {"entities" : qUnion([Q0]), "radius" : 2 * mm, "tangentPropagation" : true, "allowEdgeOverflow" : false});
        }
        {
            var Q0;
            {var subQ0=sQuery(id+"F0.wireOp",EDGE,"E22.filletArc");var subQ1=sQuery(id+"F0.wireOp",EDGE,"E7");var subQ2=sQuery(id+"F0.wireOp",EDGE,"E6");var subQ3=sQuery(id+"F0.wireOp",EDGE,"E5");var subQ4=sQuery(id+"F0.wireOp",EDGE,"E4");var subQ5=sQuery(id+"F0.wireOp",EDGE,"E1.bottom");var subQ6=sQuery(id+"F0.wireOp",EDGE,"E21.filletArc");var subQ7=sQuery(id+"F0.wireOp",EDGE,"E1.top");var subQ8=sQuery(id+"F0.wireOp",EDGE,"E1.left");var subQ9=sQuery(id+"F0.wireOp",EDGE,"E1.right");var subQ10=sQuery(id+"F0.wireOp",EDGE,"E23.filletArc");var subQ11=sQuery(id+"F0.wireOp",EDGE,"E24.filletArc");Q0=makeQuery(id+"F2.boolean.opBoolean","SPLIT",FACE,{"disambiguationData":[TD([makeQuery(id+"F1.opExtrude","SWEPT_FACE",FACE,{"disambiguationData":[OSD([subQ5])]})])],"derivedFrom":makeQuery(id+"F1.opExtrude","CAP_FACE",FACE,{"disambiguationData":[OSD([subQ5,subQ7,subQ8,subQ9,subQ4,subQ3,subQ2,subQ1,subQ6,subQ0,subQ10,subQ11])],"isStart":true})});}
            var sketch = newSketch(context, id + "F16", { "sketchPlane" : qUnion([Q0])});
            skLineSegment(sketch, "E79", {"start": v(-74.25, 0) * mm, "end": v(74.25, 0) * mm, "construction": true});
            skLineSegment(sketch, "E80", {"start": v(-1.26, 104.25) * mm, "end": v(-1.26, 74.25) * mm, "construction": true});
            skLineSegment(sketch, "E81.MirrorCS", {"start": v(12.22, 92.25) * mm, "end": v(30.22, 74.25) * mm});
            skLineSegment(sketch, "E82", {"start": v(-14.74, 92.25) * mm, "end": v(-14.74, 110.83) * mm});
            skLineSegment(sketch, "E83", {"start": v(12.22, 92.25) * mm, "end": v(12.22, 110.83) * mm});
            skArc(sketch, "E84", {"start": v(12.22, 110.83) * mm, "mid": v(-1.26, 119.25) * mm, "end": v(-14.74, 110.83) * mm});
            skLineSegment(sketch, "E85", {"start": v(-14.74, 92.25) * mm, "end": v(-32.74, 74.25) * mm});
            skCircle(sketch, "E86", {"center": v(-1.26, 104.25) * mm, "radius": 6 * mm});
            skLineSegment(sketch, "E87.MirrorCS", {"start": v(-14.74, -92.25) * mm, "end": v(-32.74, -74.25) * mm});
            skLineSegment(sketch, "E88.MirrorCS", {"start": v(-14.74, -92.25) * mm, "end": v(-14.74, -110.83) * mm});
            skCircle(sketch, "E89.MirrorC", {"center": v(-1.26, -104.25) * mm, "radius": 6 * mm});
            skLineSegment(sketch, "E90.MirrorCS", {"start": v(12.22, -92.25) * mm, "end": v(12.22, -110.83) * mm});
            skArc(sketch, "E91.MirrorCS", {"start": v(12.22, -110.83) * mm, "mid": v(-1.26, -119.25) * mm, "end": v(-14.74, -110.83) * mm});
            skLineSegment(sketch, "E92.MirrorCS", {"start": v(12.22, -92.25) * mm, "end": v(30.22, -74.25) * mm});
            skSolve(sketch);
        }
        {
            var Q0;
            {var subQ0=sQuery(id+"F16.wireOp",EDGE,"E87.MirrorCS");Q0=makeQuery(id+"F16.imprint","IMPRINT",FACE,{"disambiguationData":[TD([[makeQuery(id+"F16.imprint","IMPRINT",EDGE,{"derivedFrom":subQ0}),-1.0]])]});}
            var Q1;
            Q1=makeQuery(id+"F16.imprint","IMPRINT",FACE,{"disambiguationData":[TD([[makeQuery(id+"F16.imprint","IMPRINT",EDGE,{"derivedFrom":makeQuery(id+"F1.opExtrude","CAP_EDGE",EDGE,{"disambiguationData":[OSD([sQuery(id+"F0.wireOp",EDGE,"E1.left")])],"isStart":true})}),-1.0]])]});
            var Q2;
            {var subQ0=sQuery(id+"F16.wireOp",EDGE,"E81.MirrorCS");Q2=makeQuery(id+"F16.imprint","IMPRINT",FACE,{"disambiguationData":[TD([[makeQuery(id+"F16.imprint","IMPRINT",EDGE,{"derivedFrom":subQ0}),-1.0]])]});}
            var Q3;
            Q3=makeQuery(id+"F2.opExtrude","CAP_FACE",FACE,{"disambiguationData":[OSD([sQuery(id+"F0.wireOp",EDGE,"E12"),sQuery(id+"F0.wireOp",EDGE,"E13"),sQuery(id+"F0.wireOp",EDGE,"E14"),sQuery(id+"F0.wireOp",EDGE,"E15"),sQuery(id+"F0.wireOp",EDGE,"E17.filletArc"),sQuery(id+"F0.wireOp",EDGE,"E18.filletArc"),sQuery(id+"F0.wireOp",EDGE,"E19.filletArc"),sQuery(id+"F0.wireOp",EDGE,"E20.filletArc"),sQuery(id+"F0.wireOp",EDGE,"E25.0"),sQuery(id+"F0.wireOp",EDGE,"E25.1"),sQuery(id+"F0.wireOp",EDGE,"E25.2"),sQuery(id+"F0.wireOp",EDGE,"E25.3"),sQuery(id+"F0.wireOp",EDGE,"E25.4"),sQuery(id+"F0.wireOp",EDGE,"E25.5"),sQuery(id+"F0.wireOp",EDGE,"E25.6"),sQuery(id+"F0.wireOp",EDGE,"E25.7")])],"isStart":false});
            extrude(context, id + "F17", {"entities" : qUnion([Q0, Q1, Q2]), "operationType" : NewBodyOperationType.ADD, "endBound" : BoundingType.UP_TO_SURFACE, "endBoundEntityFace" : qUnion([Q3]), "depth" : 25 * mm});
        }
    });
